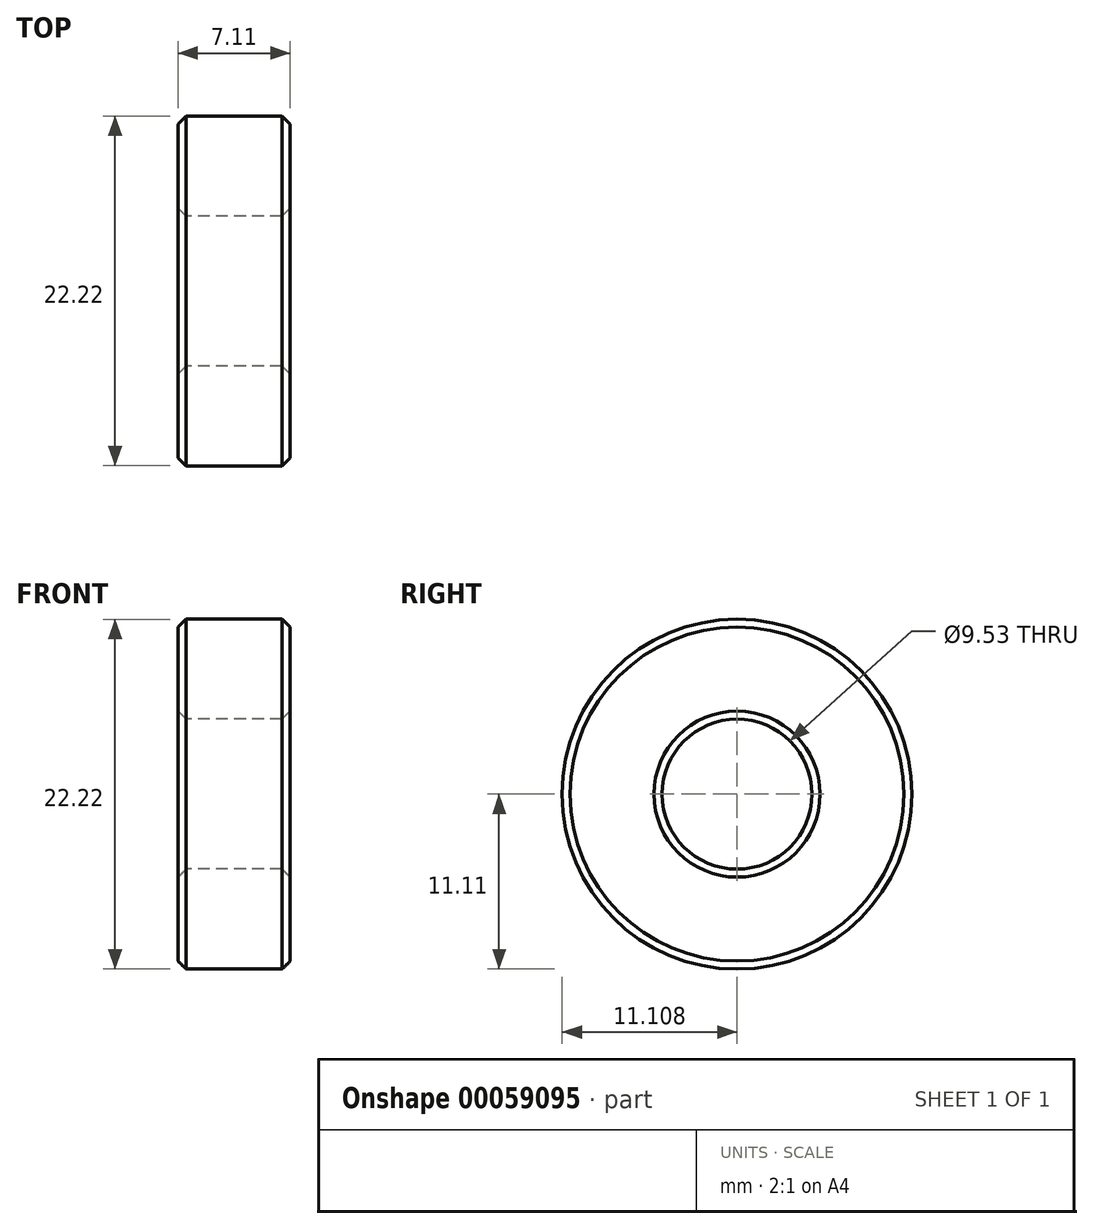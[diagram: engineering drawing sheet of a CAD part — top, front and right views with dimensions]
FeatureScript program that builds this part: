
annotation { "Feature Type Name" : "Feature", "Feature Type Description" : "" }
export const myFeature = defineFeature(function(context is Context, id is Id, definition is map)
    precondition{}
    {
        {
            var Q0;
            Q0=qCreatedBy(makeId("Right.planeOp"),FACE);
            var sketch = newSketch(context, id + "F0", { "sketchPlane" : qUnion([Q0])});
            skCircle(sketch, "E0", {"center": v(-52.88, 0) * mm, "radius": 11.11 * mm});
            skCircle(sketch, "E1", {"center": v(-52.88, 0) * mm, "radius": 4.76 * mm});
            skSolve(sketch);
        }
        {
            var Q0;
            Q0=makeQuery(id+"F0.imprint","IMPRINT",FACE,{"disambiguationData":[TD([[makeQuery(id+"F0.imprint","IMPRINT",EDGE,{"derivedFrom":sQuery(id+"F0.wireOp",EDGE,"E0")}),1.0]])]});
            extrude(context, id + "F1", {"entities" : qUnion([Q0]), "depth" : 7.11 * mm});
        }
        {
            var Q0;
            Q0=makeQuery(id+"F1.opExtrude","CAP_EDGE",EDGE,{"disambiguationData":[OSD([sQuery(id+"F0.wireOp",EDGE,"E0")])],"isStart":false});
            var Q1;
            Q1=makeQuery(id+"F1.opExtrude","CAP_EDGE",EDGE,{"disambiguationData":[OSD([sQuery(id+"F0.wireOp",EDGE,"E1")])],"isStart":false});
            var Q2;
            Q2=makeQuery(id+"F1.opExtrude","CAP_EDGE",EDGE,{"disambiguationData":[OSD([sQuery(id+"F0.wireOp",EDGE,"E0")])],"isStart":true});
            var Q3;
            Q3=makeQuery(id+"F1.opExtrude","CAP_EDGE",EDGE,{"disambiguationData":[OSD([sQuery(id+"F0.wireOp",EDGE,"E1")])],"isStart":true});
            chamfer(context, id + "F2", {"entities" : qUnion([Q0, Q1, Q2, Q3]), "width" : 0.5 * mm, "tangentPropagation" : true});
        }
    });
